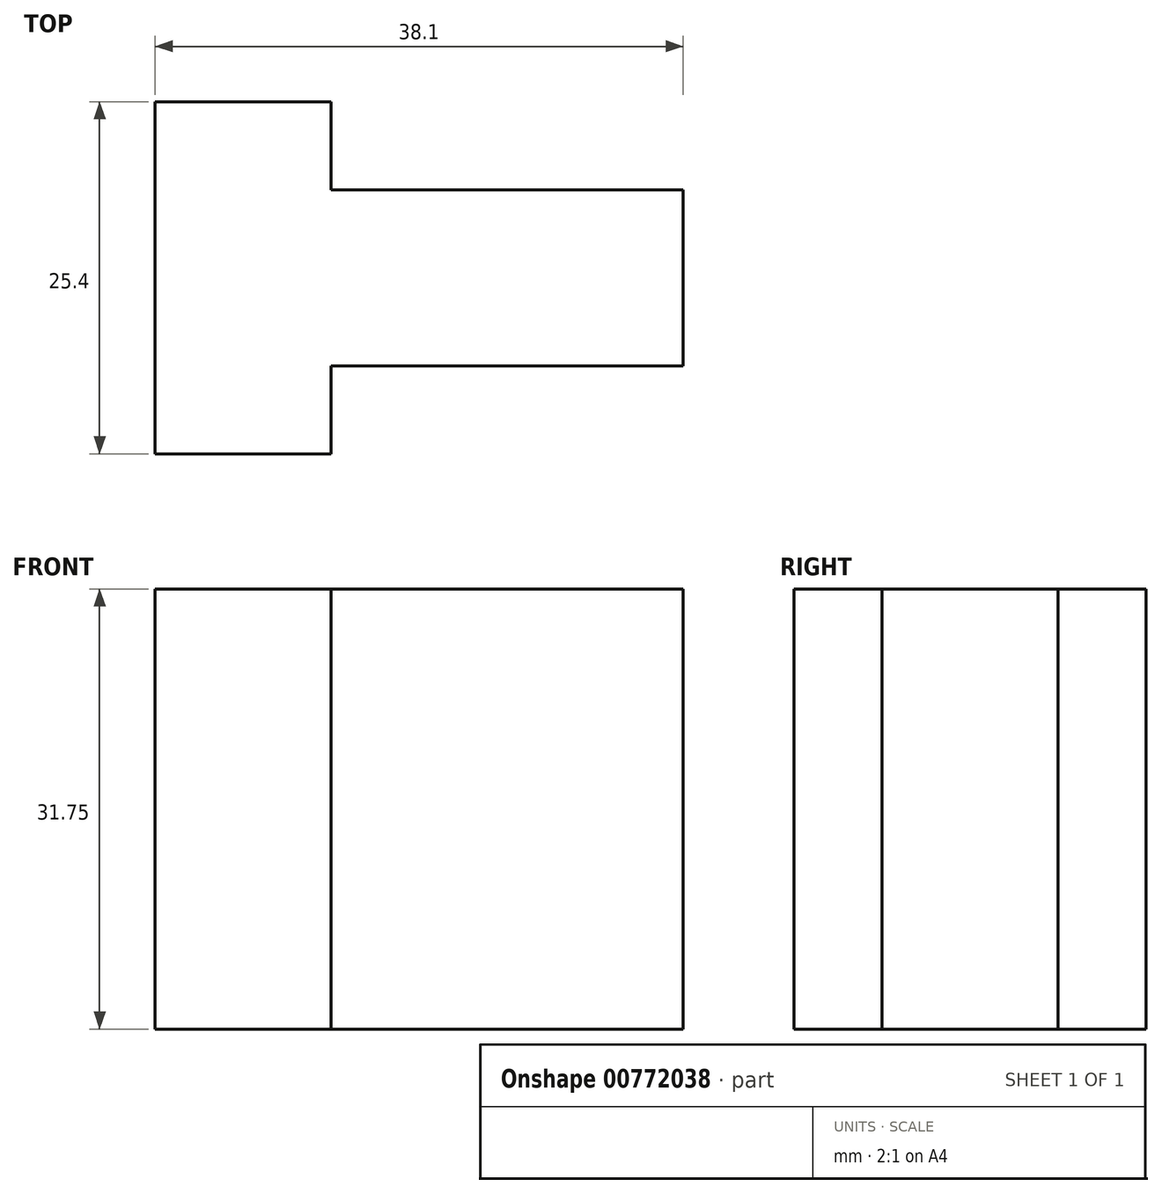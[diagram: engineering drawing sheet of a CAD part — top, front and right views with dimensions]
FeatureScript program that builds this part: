
annotation { "Feature Type Name" : "Feature", "Feature Type Description" : "" }
export const myFeature = defineFeature(function(context is Context, id is Id, definition is map)
    precondition{}
    {
        {
            var Q0;
            Q0=qCreatedBy(makeId("Top.planeOp"),FACE);
            var sketch = newSketch(context, id + "F0", { "sketchPlane" : qUnion([Q0])});
            skLineSegment(sketch, "E0", {"start": v(0, 0) * mm, "end": v(25.4, 0) * mm});
            skLineSegment(sketch, "E1", {"start": v(25.4, 0) * mm, "end": v(25.4, 12.7) * mm});
            skLineSegment(sketch, "E2", {"start": v(25.4, 12.7) * mm, "end": v(0, 12.7) * mm});
            skLineSegment(sketch, "E3", {"start": v(0, 12.7) * mm, "end": v(0, 19.05) * mm});
            skLineSegment(sketch, "E4", {"start": v(0, 19.05) * mm, "end": v(-12.7, 19.05) * mm});
            skLineSegment(sketch, "E5", {"start": v(0, 0) * mm, "end": v(0, -6.35) * mm});
            skLineSegment(sketch, "E6", {"start": v(0, -6.35) * mm, "end": v(-12.7, -6.35) * mm});
            skLineSegment(sketch, "E7", {"start": v(-12.7, 19.05) * mm, "end": v(-12.7, -6.35) * mm});
            skSolve(sketch);
        }
        {
            var Q0;
            Q0 = qSketchRegion(id + "F0", true);
            extrude(context, id + "F1", {"entities" : qUnion([Q0]), "depth" : 31.75 * mm, "offsetDistance" : 25.4 * mm});
        }
    });
